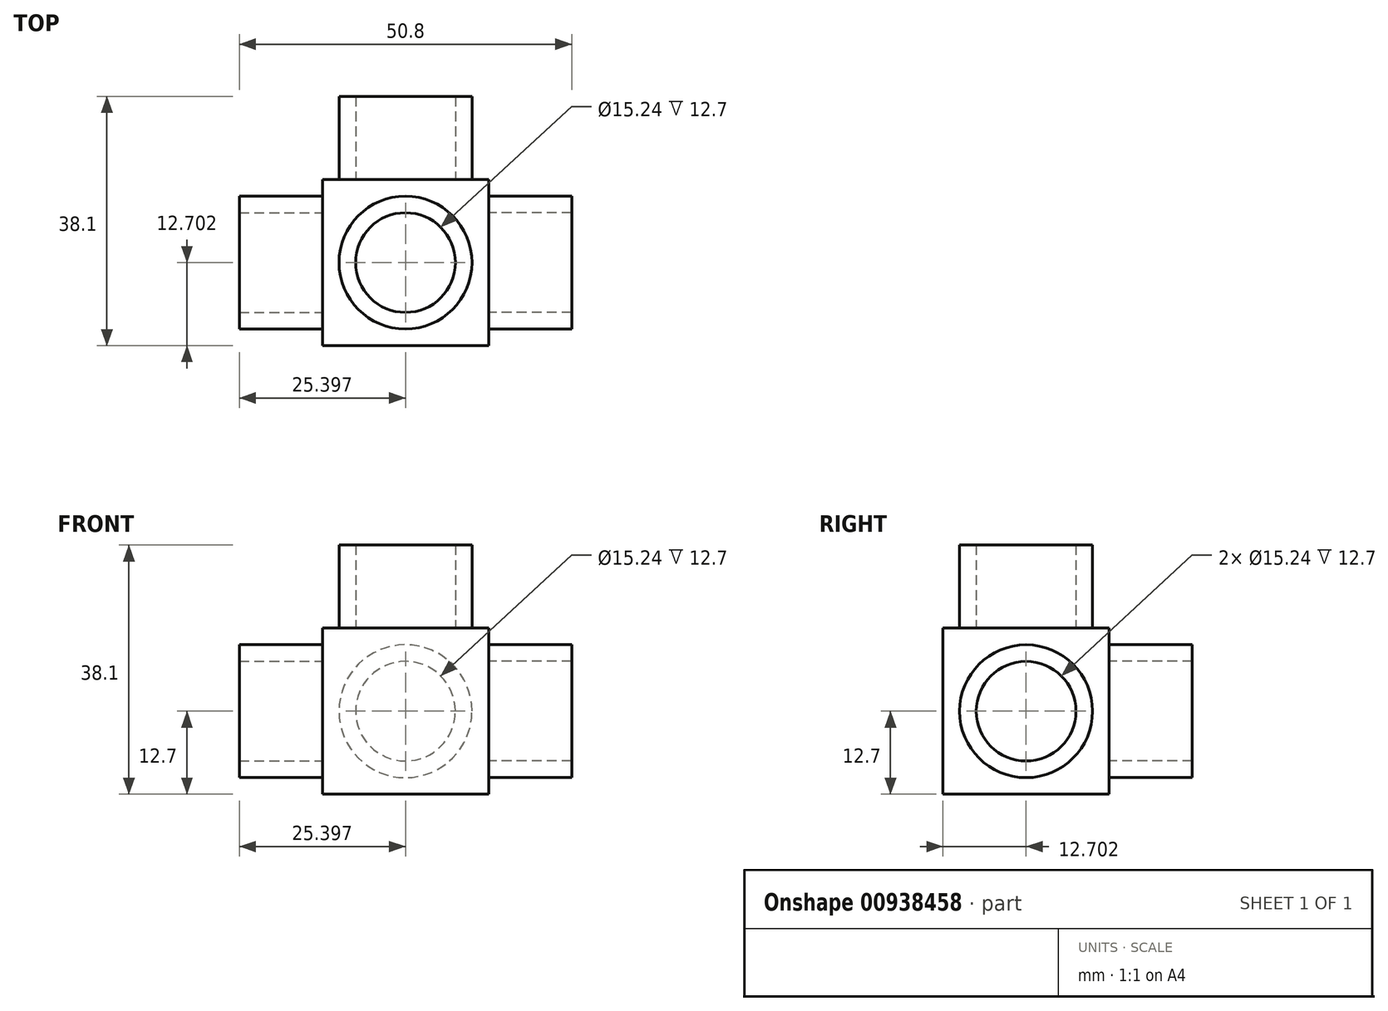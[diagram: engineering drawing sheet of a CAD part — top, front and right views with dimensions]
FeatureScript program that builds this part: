
annotation { "Feature Type Name" : "Feature", "Feature Type Description" : "" }
export const myFeature = defineFeature(function(context is Context, id is Id, definition is map)
    precondition{}
    {
        {
            var Q0;
            Q0=qCreatedBy(makeId("Top.planeOp"),FACE);
            var sketch = newSketch(context, id + "F0", { "sketchPlane" : qUnion([Q0])});
            skLineSegment(sketch, "E0.bottom", {"start": v(-22.02, 17.34) * mm, "end": v(-47.42, 17.34) * mm});
            skLineSegment(sketch, "E0.top", {"start": v(-22.02, 42.74) * mm, "end": v(-47.42, 42.74) * mm});
            skLineSegment(sketch, "E0.left", {"start": v(-22.02, 17.34) * mm, "end": v(-22.02, 42.74) * mm});
            skLineSegment(sketch, "E0.right", {"start": v(-47.42, 17.34) * mm, "end": v(-47.42, 42.74) * mm});
            skPoint(sketch, "E0.middle", {"position": v(-34.72, 30.04) * mm});
            skSolve(sketch);
        }
        {
            var Q0;
            Q0=makeQuery(id+"F0.imprint","IMPRINT",FACE,{"disambiguationData":[TD([[makeQuery(id+"F0.imprint","IMPRINT",EDGE,{"derivedFrom":sQuery(id+"F0.wireOp",EDGE,"E0.bottom")}),-1.0]])]});
            extrude(context, id + "F1", {"entities" : qUnion([Q0]), "depth" : 25.4 * mm, "offsetDistance" : 25.4 * mm});
        }
        {
            var Q0;
            Q0=makeQuery(id+"F1.opExtrude","SWEPT_FACE",FACE,{"disambiguationData":[OSD([sQuery(id+"F0.wireOp",EDGE,"E0.left")])]});
            var sketch = newSketch(context, id + "F2", { "sketchPlane" : qUnion([Q0])});
            skLineSegment(sketch, "E1", {"start": v(42.74, 25.4) * mm, "end": v(17.34, 0) * mm, "construction": true});
            skCircle(sketch, "E2", {"center": v(30.04, 12.7) * mm, "radius": 7.62 * mm});
            skCircle(sketch, "E3", {"center": v(30.04, 12.7) * mm, "radius": 10.16 * mm});
            skSolve(sketch);
        }
        {
            var Q0;
            Q0=makeQuery(id+"F1.opExtrude","SWEPT_FACE",FACE,{"disambiguationData":[OSD([sQuery(id+"F0.wireOp",EDGE,"E0.top")])]});
            var sketch = newSketch(context, id + "F3", { "sketchPlane" : qUnion([Q0])});
            skLineSegment(sketch, "E4", {"start": v(47.42, 25.4) * mm, "end": v(22.02, 0) * mm, "construction": true});
            skCircle(sketch, "E5", {"center": v(34.72, 12.7) * mm, "radius": 7.62 * mm});
            skCircle(sketch, "E6", {"center": v(34.72, 12.7) * mm, "radius": 10.16 * mm});
            skSolve(sketch);
        }
        {
            var Q0;
            Q0 = qSketchRegion(id + "F3", true);
            extrude(context, id + "F4", {"entities" : qUnion([Q0]), "operationType" : NewBodyOperationType.ADD, "depth" : 12.7 * mm, "offsetDistance" : 25.4 * mm});
        }
        {
            var Q0;
            Q0=makeQuery(id+"F1.opExtrude","CAP_FACE",FACE,{"disambiguationData":[OSD([sQuery(id+"F0.wireOp",EDGE,"E0.bottom"),sQuery(id+"F0.wireOp",EDGE,"E0.top"),sQuery(id+"F0.wireOp",EDGE,"E0.left"),sQuery(id+"F0.wireOp",EDGE,"E0.right")])],"isStart":false});
            var sketch = newSketch(context, id + "F5", { "sketchPlane" : qUnion([Q0])});
            skLineSegment(sketch, "E7", {"start": v(-22.02, 42.74) * mm, "end": v(-47.42, 17.34) * mm, "construction": true});
            skCircle(sketch, "E8", {"center": v(-34.72, 30.04) * mm, "radius": 7.62 * mm});
            skCircle(sketch, "E9", {"center": v(-34.72, 30.04) * mm, "radius": 10.16 * mm});
            skSolve(sketch);
        }
        {
            var Q0;
            Q0=makeQuery(id+"F1.opExtrude","SWEPT_FACE",FACE,{"disambiguationData":[OSD([sQuery(id+"F0.wireOp",EDGE,"E0.right")])]});
            var sketch = newSketch(context, id + "F6", { "sketchPlane" : qUnion([Q0])});
            skLineSegment(sketch, "E10", {"start": v(-17.34, 25.4) * mm, "end": v(-42.74, 0) * mm, "construction": true});
            skCircle(sketch, "E11", {"center": v(-30.04, 12.7) * mm, "radius": 7.62 * mm});
            skCircle(sketch, "E12", {"center": v(-30.04, 12.7) * mm, "radius": 10.16 * mm});
            skSolve(sketch);
        }
        {
            var Q0;
            Q0 = qSketchRegion(id + "F5", true);
            extrude(context, id + "F7", {"entities" : qUnion([Q0]), "operationType" : NewBodyOperationType.ADD, "depth" : 12.7 * mm, "offsetDistance" : 25.4 * mm});
        }
        {
            var Q0;
            Q0 = qSketchRegion(id + "F6", true);
            extrude(context, id + "F8", {"entities" : qUnion([Q0]), "operationType" : NewBodyOperationType.ADD, "depth" : 12.7 * mm, "offsetDistance" : 25.4 * mm});
        }
        {
            var Q0;
            Q0=makeQuery(id+"F2.imprint","IMPRINT",FACE,{"disambiguationData":[TD([[makeQuery(id+"F2.imprint","IMPRINT",EDGE,{"derivedFrom":sQuery(id+"F2.wireOp",EDGE,"E2")}),-1.0]])]});
            extrude(context, id + "F9", {"entities" : qUnion([Q0]), "operationType" : NewBodyOperationType.ADD, "depth" : 12.7 * mm, "offsetDistance" : 25.4 * mm});
        }
    });
